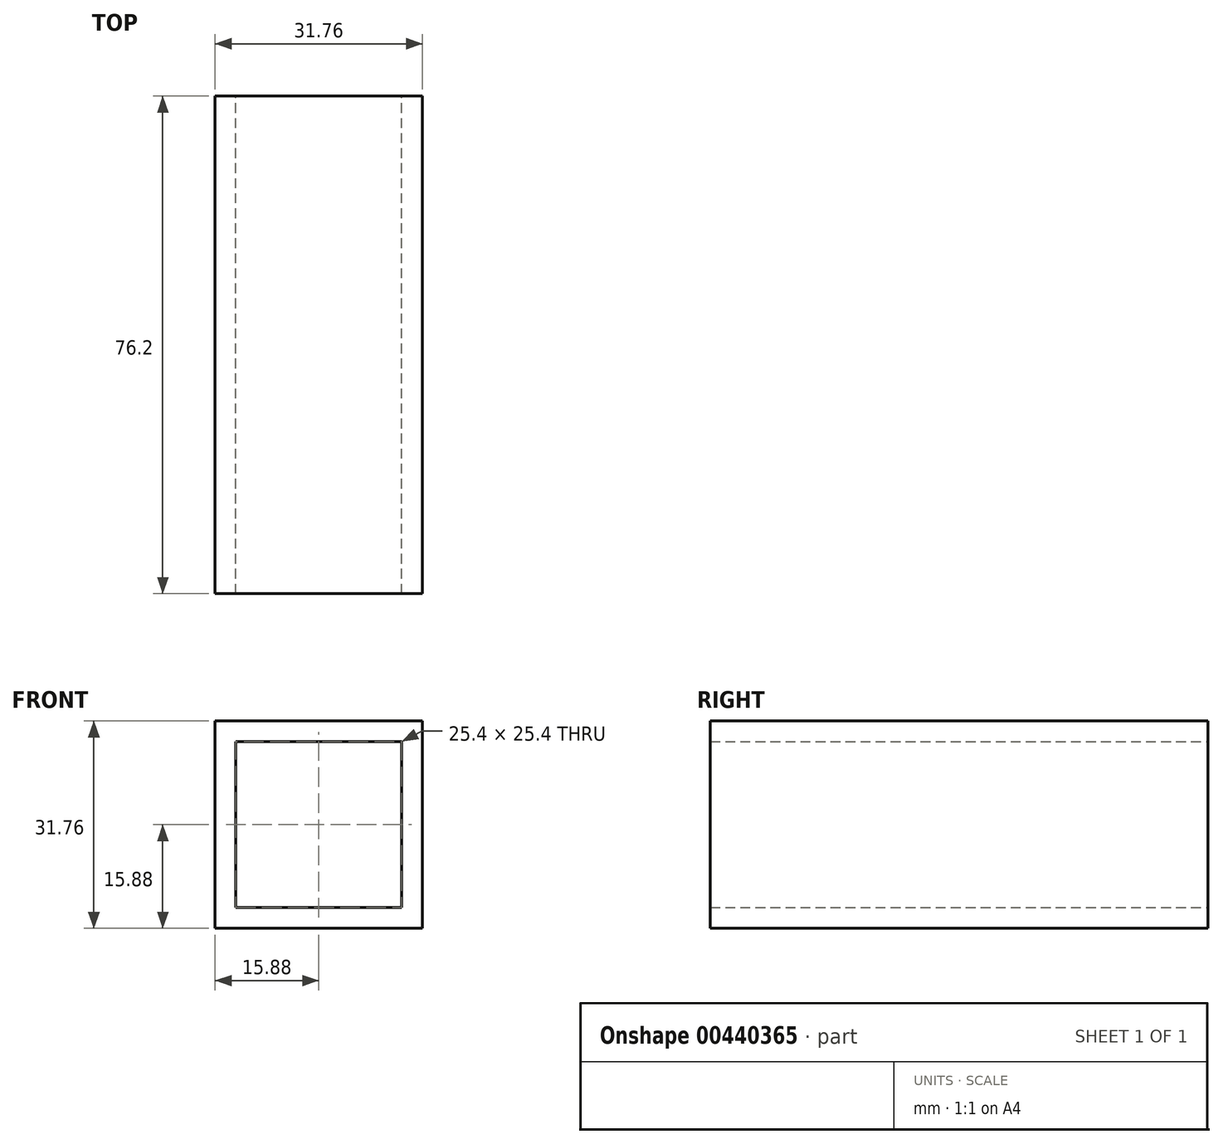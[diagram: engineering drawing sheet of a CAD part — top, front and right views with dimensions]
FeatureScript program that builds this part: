
annotation { "Feature Type Name" : "Feature", "Feature Type Description" : "" }
export const myFeature = defineFeature(function(context is Context, id is Id, definition is map)
    precondition{}
    {
        {
            var Q0;
            Q0=qCreatedBy(makeId("Front.planeOp"),FACE);
            var sketch = newSketch(context, id + "F0", { "sketchPlane" : qUnion([Q0])});
            skLineSegment(sketch, "E0.bottom", {"start": v(-15.87, 15.88) * mm, "end": v(15.88, 15.88) * mm});
            skLineSegment(sketch, "E0.top", {"start": v(-15.88, -15.88) * mm, "end": v(15.87, -15.88) * mm});
            skLineSegment(sketch, "E0.left", {"start": v(-15.87, 15.88) * mm, "end": v(-15.88, -15.88) * mm});
            skLineSegment(sketch, "E0.right", {"start": v(15.88, 15.88) * mm, "end": v(15.87, -15.88) * mm});
            skPoint(sketch, "E0.middle", {"position": v(0, 0) * mm});
            skLineSegment(sketch, "E1.bottom", {"start": v(-12.7, 12.7) * mm, "end": v(12.7, 12.7) * mm});
            skLineSegment(sketch, "E1.top", {"start": v(-12.7, -12.7) * mm, "end": v(12.7, -12.7) * mm});
            skLineSegment(sketch, "E1.left", {"start": v(-12.7, 12.7) * mm, "end": v(-12.7, -12.7) * mm});
            skLineSegment(sketch, "E1.right", {"start": v(12.7, 12.7) * mm, "end": v(12.7, -12.7) * mm});
            skSolve(sketch);
        }
        {
            var Q0;
            Q0=makeQuery(id+"F0.imprint","IMPRINT",FACE,{"disambiguationData":[TD([[makeQuery(id+"F0.imprint","IMPRINT",EDGE,{"derivedFrom":sQuery(id+"F0.wireOp",EDGE,"E0.bottom")}),-1.0]])]});
            extrude(context, id + "F1", {"entities" : qUnion([Q0]), "endBound" : BoundingType.SYMMETRIC, "depth" : 76.2 * mm});
        }
    });
